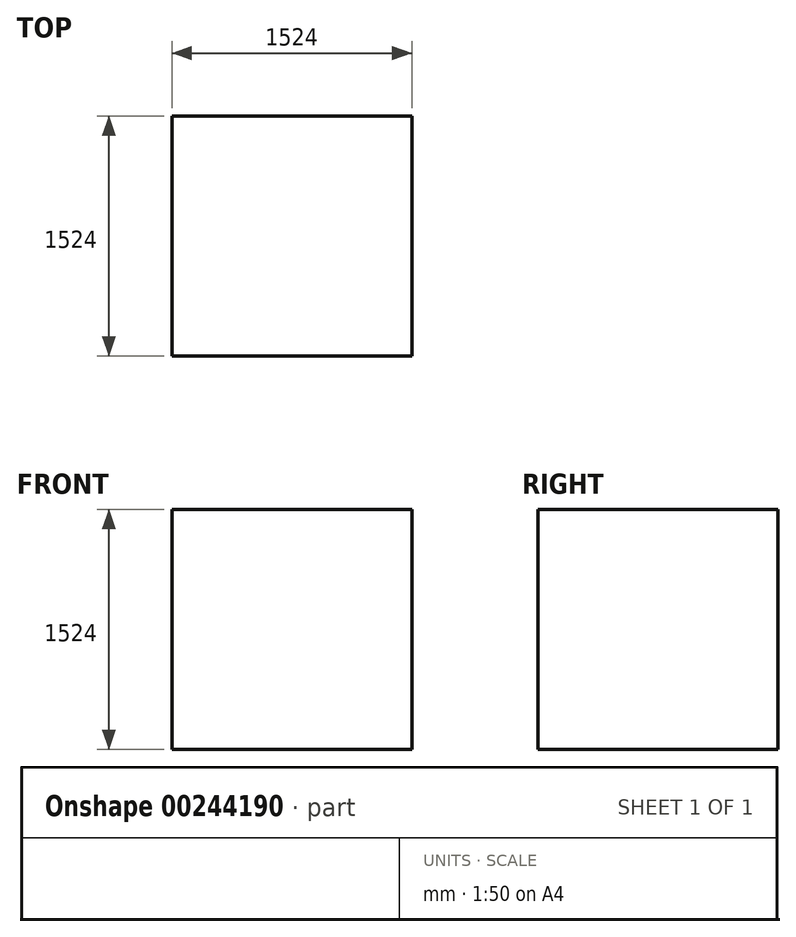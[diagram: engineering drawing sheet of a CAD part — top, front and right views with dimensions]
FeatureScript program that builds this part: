
annotation { "Feature Type Name" : "Feature", "Feature Type Description" : "" }
export const myFeature = defineFeature(function(context is Context, id is Id, definition is map)
    precondition{}
    {
        {
            var Q0;
            Q0=qCreatedBy(makeId("Top.planeOp"),FACE);
            var sketch = newSketch(context, id + "F0", { "sketchPlane" : qUnion([Q0])});
            skLineSegment(sketch, "E0.bottom", {"start": v(732.02, -767.27) * mm, "end": v(-791.98, -767.27) * mm});
            skLineSegment(sketch, "E0.top", {"start": v(732.02, 756.73) * mm, "end": v(-791.98, 756.73) * mm});
            skLineSegment(sketch, "E0.left", {"start": v(732.02, -767.27) * mm, "end": v(732.02, 756.73) * mm});
            skLineSegment(sketch, "E0.right", {"start": v(-791.98, -767.27) * mm, "end": v(-791.98, 756.73) * mm});
            skSolve(sketch);
        }
        {
            var Q0;
            Q0=makeQuery(id+"F0.imprint","IMPRINT",FACE,{"disambiguationData":[TD([[makeQuery(id+"F0.imprint","IMPRINT",EDGE,{"derivedFrom":sQuery(id+"F0.wireOp",EDGE,"E0.bottom")}),-1.0]])]});
            extrude(context, id + "F1", {"entities" : qUnion([Q0]), "depth" : 1524 * mm});
        }
    });
